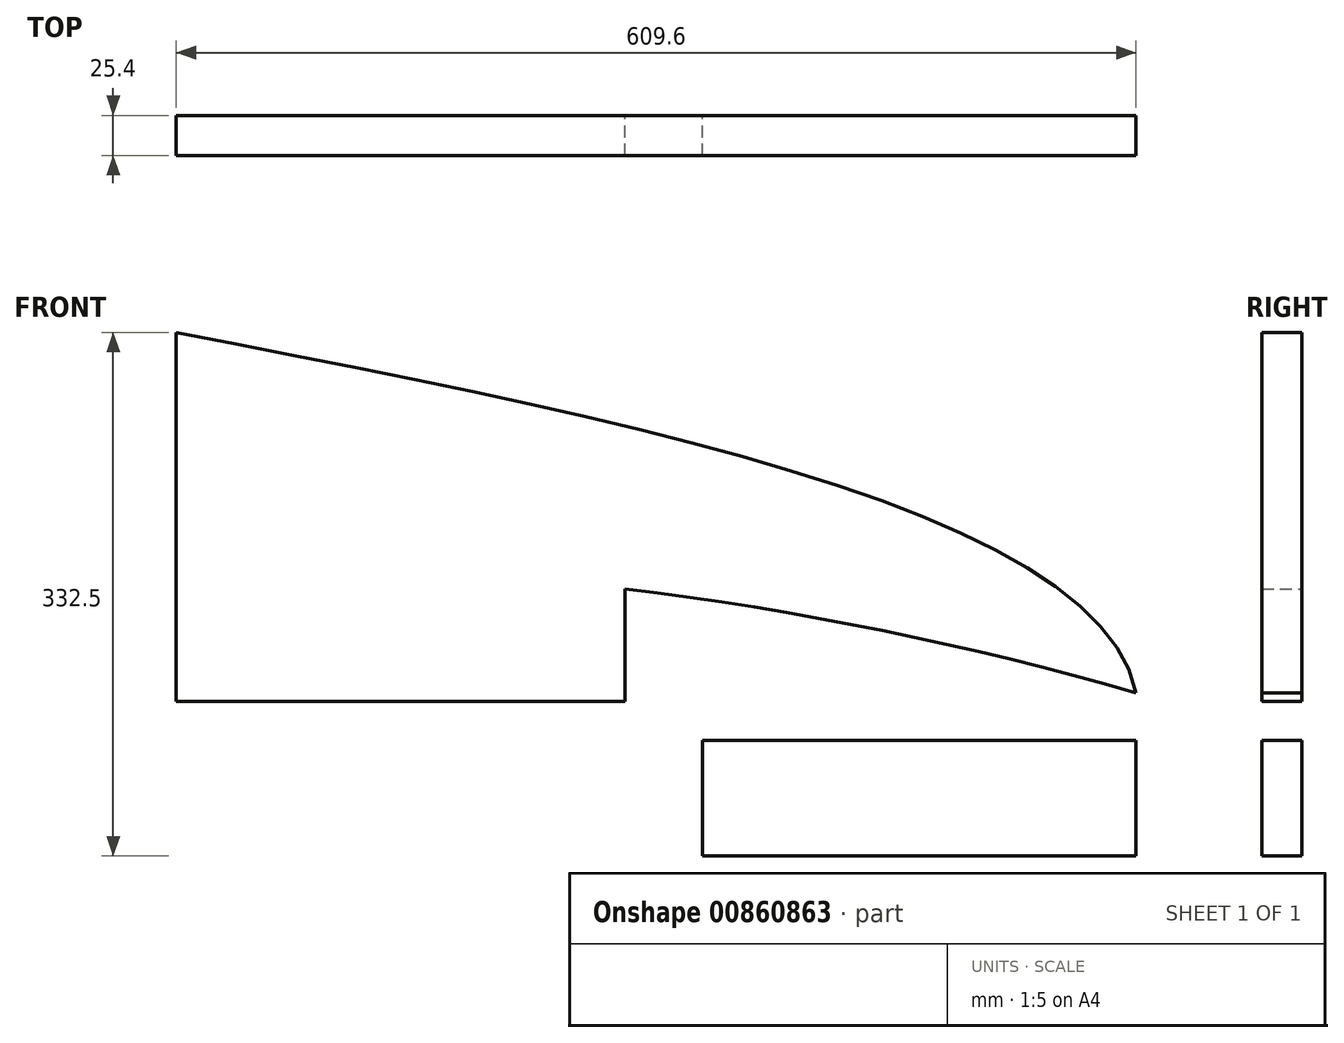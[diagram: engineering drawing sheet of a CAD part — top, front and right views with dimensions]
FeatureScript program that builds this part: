
annotation { "Feature Type Name" : "Feature", "Feature Type Description" : "" }
export const myFeature = defineFeature(function(context is Context, id is Id, definition is map)
    precondition{}
    {
        {
            var Q0;
            Q0=qCreatedBy(makeId("Front.planeOp"),FACE);
            var sketch = newSketch(context, id + "F0", { "sketchPlane" : qUnion([Q0])});
            skLineSegment(sketch, "E0.left", {"start": v(-285.14, 277.98) * mm, "end": v(-285.14, 129.6) * mm});
            skFitSpline(sketch, "E1", {"points": [v(-285.14, 277.98) * mm, v(324.46, 49.16) * mm, v(-163.57, -428.15) * mm], "startDerivative": vector(1776.9, -344.45) * mm, "endDerivative": vector(-1520.78, -1064.98) * mm});
            skArc(sketch, "E2", {"start": v(324.46, 49.16) * mm, "mid": v(22.68, 112.27) * mm, "end": v(-285.14, 129.6) * mm});
            skLineSegment(sketch, "E3.top", {"start": v(-285.14, 43.8) * mm, "end": v(0, 43.8) * mm});
            skLineSegment(sketch, "E3.left", {"start": v(-285.14, 129.6) * mm, "end": v(-285.14, 43.8) * mm});
            skLineSegment(sketch, "E3.right", {"start": v(0, 115.13) * mm, "end": v(0, 43.8) * mm});
            skLineSegment(sketch, "E4.bottom", {"start": v(324.46, 18.77) * mm, "end": v(49.16, 18.77) * mm});
            skLineSegment(sketch, "E4.top", {"start": v(324.46, -54.52) * mm, "end": v(49.16, -54.52) * mm});
            skLineSegment(sketch, "E4.left", {"start": v(324.46, 18.77) * mm, "end": v(324.46, -54.52) * mm});
            skLineSegment(sketch, "E4.right", {"start": v(49.16, 18.77) * mm, "end": v(49.16, -54.52) * mm});
            skSolve(sketch);
        }
        {
            var Q0;
            Q0 = qSketchRegion(id + "F0", true);
            extrude(context, id + "F1", {"entities" : qUnion([Q0]), "depth" : 25.4 * mm, "offsetDistance" : 25.4 * mm});
        }
    });
